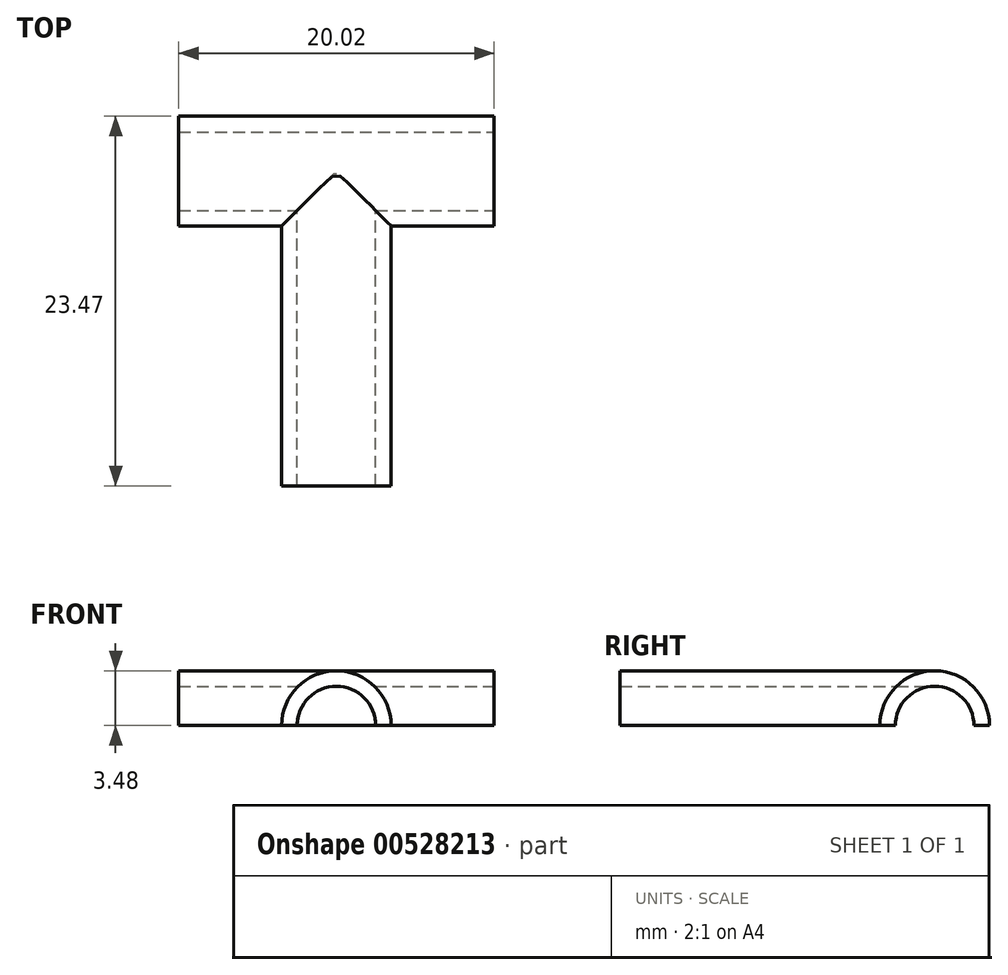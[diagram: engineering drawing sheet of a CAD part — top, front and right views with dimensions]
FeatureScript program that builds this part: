
annotation { "Feature Type Name" : "Feature", "Feature Type Description" : "" }
export const myFeature = defineFeature(function(context is Context, id is Id, definition is map)
    precondition{}
    {
        {
            var Q0;
            Q0=qCreatedBy(makeId("Front.planeOp"),FACE);
            var sketch = newSketch(context, id + "F0", { "sketchPlane" : qUnion([Q0])});
            skCircle(sketch, "E0", {"center": v(0, 0) * mm, "radius": 3.48 * mm});
            skLineSegment(sketch, "E1", {"start": v(0, 0) * mm, "end": v(-3.48, 0) * mm});
            skLineSegment(sketch, "E2", {"start": v(-3.48, 0) * mm, "end": v(3.48, 0) * mm});
            skSolve(sketch);
        }
        {
            var Q0;
            Q0=qCreatedBy(makeId("Right.planeOp"),FACE);
            var sketch = newSketch(context, id + "F1", { "sketchPlane" : qUnion([Q0])});
            skCircle(sketch, "E3", {"center": v(0, 0) * mm, "radius": 3.48 * mm});
            skLineSegment(sketch, "E4", {"start": v(0, 0) * mm, "end": v(3.48, 0) * mm});
            skLineSegment(sketch, "E5", {"start": v(3.48, 0) * mm, "end": v(-3.48, 0) * mm});
            skSolve(sketch);
        }
        {
            var Q0;
            {var subQ0=sQuery(id+"F0.wireOp",EDGE,"E2");var subQ4=makeQuery(id+"F0.imprint","IMPRINT",VERTEX,{"derivedFrom":subQ0});Q0=makeQuery(id+"F0.imprint","IMPRINT",FACE,{"disambiguationData":[TD([[makeQuery(id+"F0.imprint","IMPRINT",EDGE,{"disambiguationData":[TD([[subQ4,1.0]])],"derivedFrom":subQ0}),1.0]])]});}
            extrude(context, id + "F2", {"entities" : qUnion([Q0]), "depth" : 19.99 * mm, "offsetDistance" : 25.4 * mm});
        }
        {
            var Q0;
            {var subQ0=sQuery(id+"F1.wireOp",EDGE,"E5");var subQ4=makeQuery(id+"F1.imprint","IMPRINT",VERTEX,{"derivedFrom":subQ0});Q0=makeQuery(id+"F1.imprint","IMPRINT",FACE,{"disambiguationData":[TD([[makeQuery(id+"F1.imprint","IMPRINT",EDGE,{"disambiguationData":[TD([[subQ4,1.0]])],"derivedFrom":subQ0}),-1.0]])]});}
            extrude(context, id + "F3", {"entities" : qUnion([Q0]), "operationType" : NewBodyOperationType.ADD, "depth" : 10 * mm, "offsetDistance" : 25.4 * mm, "hasSecondDirection" : true, "secondDirectionOppositeDirection" : true, "secondDirectionDepth" : 10 * mm});
        }
        {
            var Q0;
            Q0=qCreatedBy(makeId("Front.planeOp"),FACE);
            var sketch = newSketch(context, id + "F4", { "sketchPlane" : qUnion([Q0])});
            skCircle(sketch, "E6", {"center": v(0, 0) * mm, "radius": 2.5 * mm});
            skSolve(sketch);
        }
        {
            var Q0;
            Q0=makeQuery(id+"F4.imprint","IMPRINT",FACE,{"disambiguationData":[TD([[makeQuery(id+"F4.imprint","IMPRINT",EDGE,{"derivedFrom":sQuery(id+"F4.wireOp",EDGE,"E6")}),1.0]])]});
            extrude(context, id + "F5", {"entities" : qUnion([Q0]), "operationType" : NewBodyOperationType.REMOVE, "oppositeDirection" : true, "depth" : 0 * mm, "offsetDistance" : 25.4 * mm, "hasSecondDirection" : true, "secondDirectionOppositeDirection" : false, "secondDirectionDepth" : 25.4 * mm});
        }
        {
            var Q0;
            Q0=qCreatedBy(makeId("Right.planeOp"),FACE);
            var sketch = newSketch(context, id + "F6", { "sketchPlane" : qUnion([Q0])});
            skCircle(sketch, "E7", {"center": v(0, 0) * mm, "radius": 2.5 * mm});
            skSolve(sketch);
        }
        {
            var Q0;
            Q0=makeQuery(id+"F6.imprint","IMPRINT",FACE,{"disambiguationData":[TD([[makeQuery(id+"F6.imprint","IMPRINT",EDGE,{"derivedFrom":sQuery(id+"F6.wireOp",EDGE,"E7")}),1.0]])]});
            extrude(context, id + "F7", {"entities" : qUnion([Q0]), "operationType" : NewBodyOperationType.REMOVE, "oppositeDirection" : true, "depth" : 25.4 * mm, "offsetDistance" : 25.4 * mm, "hasSecondDirection" : true, "secondDirectionOppositeDirection" : false, "secondDirectionDepth" : 25.4 * mm});
        }
    });
